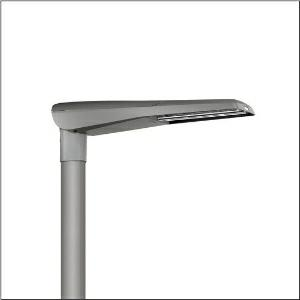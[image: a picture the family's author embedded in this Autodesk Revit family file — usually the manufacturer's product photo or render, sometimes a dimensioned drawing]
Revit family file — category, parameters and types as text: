
# Revit family: streetlight_sl_11_iq_mini___st1_0a_5xc2mc1f08ge_6161
name_source: partatom
category: Lighting Fixtures
units: mm (PartAtom-declared; Revit-internal decimal feet)

## family parameters
Cut with Voids When Loaded = No
Host = Face
Light Source = No
Part Type = Normal
Room Calculation Point = No
Round Connector Dimension = Use Diameter
Shared = No

## types (1)
- --- (1 x LED, 2940 lm, 25.3 W, 2200K)
    Apparent Load = 25 VA
    CIE Flux Codes = 33 66 96 100 100
    Color Rendering = 70
    Color Temperature = 2200K
    Default Elevation = 1800 mm
    Description = Streetlight SL 11 iQ mini, mast luminaire, primary light control with 3 zone facetted reflector, of plastic, silver coated, highly specular, primary optical cover: cover, of PMMA, transparent, light distribution: ST1.0a, light emission: direct distribution, primary light characteristic: asymmetric, installation type: post-top, side-entry, lamps: LED, High Power LED, rated values: 3.460lm | 24,9W | 139lm/W (begin service life); end service life: 3.460lm | 25,7W; at 50% lumin. flux: 1.730lm | 12,8W | 135,2lm/W, colour temperature: 2200/2700/3000/4000K, colour rendering: CRI > 70, light colour: 722/727/730/740, light setting 1 begin service life: 100% | 3.460lm | 24,9W | 139lm/W | 3.000K, light setting 1 end service life: 25,7W, further light settings possible, control: Street-Remote, Auto-Match, Temp-Guard, Lumen-Switch, Night-Set, Smart-Wire, Light-Fading, Desk-Remote (wireless, voltage-free reading and setting of iQ features in the workshop via application-optimized NFC function/RFID function), optimised constant luminous flux control (CLO 2.0), with cable H07RN-F 3x 1.5mm², mains connection: 230..240V, AC, 50/60Hz, connection cable pre-assembled, cable length: 6,5m, luminaire housing, of diecast aluminium, powder-coated, SITECO metallic grey (DB 702S), please order mast flange separately, inclination adjustable without tools: 0°, 5°, 10°, 15° (post-top) | 0°, -5°, -10°, -15° (side-entry), sealing non-destructively replaceable, multi-level sealing system, length: 736mm, width: 174mm, height: 116mm, mast flange for spigot size: 42mm (side-entry): 5XC10008XM4, 60/48mm (side-entry/post-top): 5XC10108XM2, 76/60mm (side-entry/post-top): 5XC10108XM1, equipment: standard, protection rating (complete): IP66, insulation class (complete): insulation class II (safety insulation), certification: CE, ENEC, ENEC+, VDE, impact resistance: IK10, permissible operating ambient temperature for outdoor applications: -25..+50°C, standard-compliant lighting for roads and squares, Environmental Product Declaration (EPD) tested and certified by an independent institute, packaging unit: 1 piece

Light Distribution: ST1.0a
    Height = 116 mm
    Lamp = 1 x LED
    Lamp Light Flux = 2940 lm
    Lamp Power = 25.3 W
    Lamp count = 1
    Length = 736 mm
    Luminous efficacy = 116 lm/W
    Manufacturer = Siteco
    ModVariant = No
    Model = 5XC2MC1F08GE
    Number of Poles = 1
    OnlyDefault = Yes
    Power Factor = 1
    Product Name = Streetlight SL 11 iQ mini | ST1.0a
    Product group = mast luminaire | pylon top
    ProductGroupID = 6100
    Protection Class = Protection class II
    Protection Degree = IP 66
    RLX_Detail_Level = 1
    RLX_Emergency_Light_Flux = 0 lm
    RLX_Emergency_Type = 0
    RLX_Emergency_Type_DB = No
    RlxData = <blob elided: 52793 chars, md5=3fc6546a>
    Socket = socket
    Standby Power = 0 W
    System Light Flux = 2940 lm
    System Power = 25 W
    Type Comments = individual setting: luminous flux: 100 % | dim-lin: 254 | 351 mA
    Type Image = l_1003508.jpg
    URL = http://relux.com
    VarID = @adj_042497
    Voltage = 0 V
    Weight = 0.00 kg
    Width = 174 mm

## geometry (parser evidence)
native form markers: Blend x4, Sweep x11
no freeform markers — native parametric forms only
